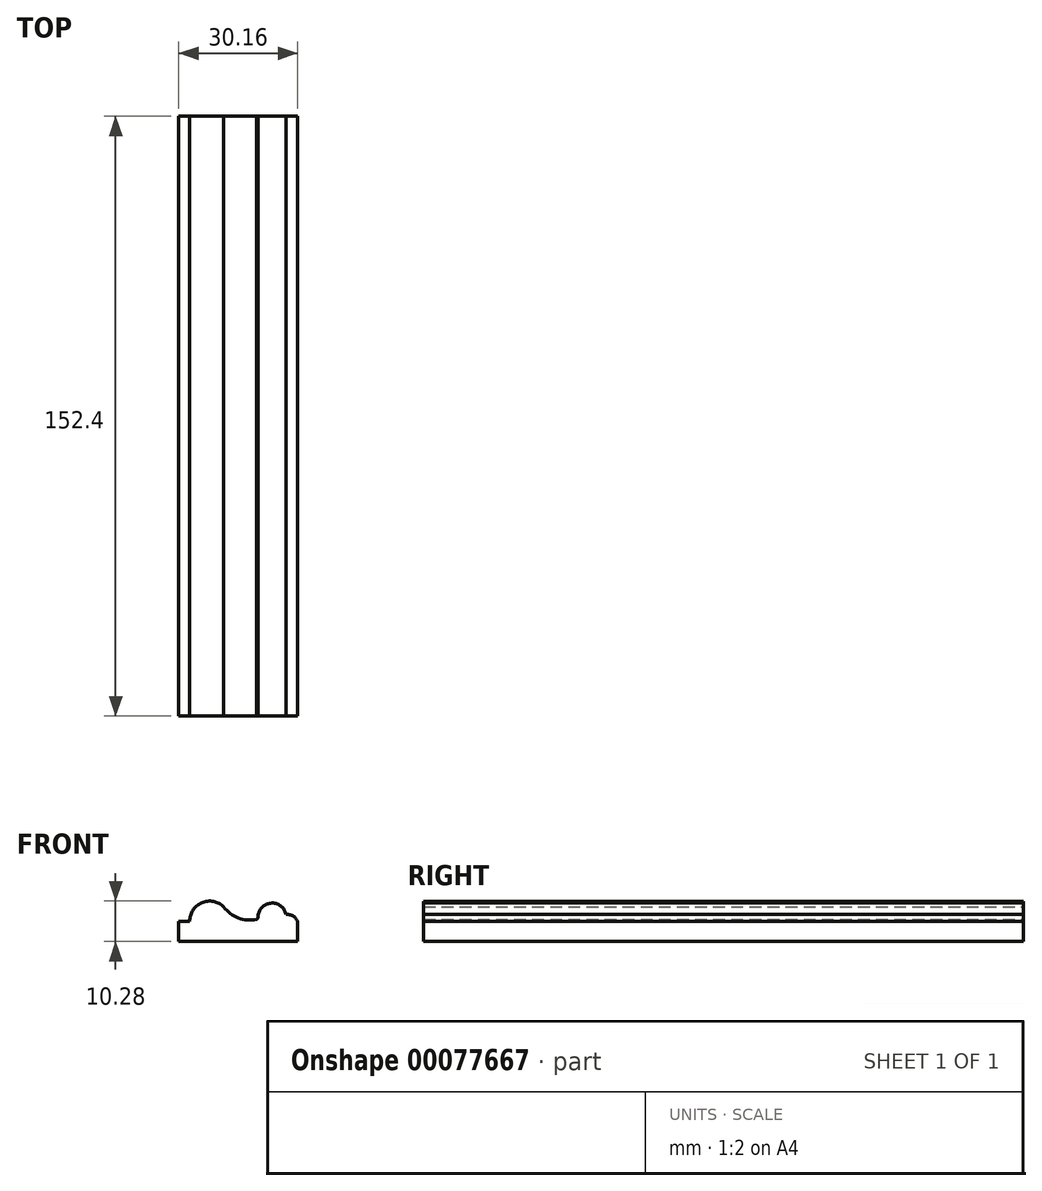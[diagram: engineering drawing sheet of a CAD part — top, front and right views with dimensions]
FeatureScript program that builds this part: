
annotation { "Feature Type Name" : "Feature", "Feature Type Description" : "" }
export const myFeature = defineFeature(function(context is Context, id is Id, definition is map)
    precondition{}
    {
        {
            var Q0;
            Q0=qCreatedBy(makeId("Front.planeOp"),FACE);
            var sketch = newSketch(context, id + "F0", { "sketchPlane" : qUnion([Q0])});
            skLineSegment(sketch, "E0", {"start": v(-15.08, -5.14) * mm, "end": v(-15.08, -0.06) * mm});
            skLineSegment(sketch, "E1", {"start": v(-15.08, -5.14) * mm, "end": v(15.08, -5.14) * mm});
            skLineSegment(sketch, "E2", {"start": v(15.08, -5.14) * mm, "end": v(15.08, 0) * mm});
            skLineSegment(sketch, "E3", {"start": v(-12.31, -0.06) * mm, "end": v(-15.08, -0.06) * mm});
            skArc(sketch, "E4", {"start": v(12.16, 1.72) * mm, "mid": v(8.26, 4.62) * mm, "end": v(5.02, 1) * mm});
            skArc(sketch, "E5", {"start": v(15.08, 0) * mm, "mid": v(13.91, 1.35) * mm, "end": v(12.16, 1.72) * mm});
            skArc(sketch, "E6", {"start": v(-3.66, 3.68) * mm, "mid": v(-9.24, 4.72) * mm, "end": v(-12.31, -0.06) * mm});
            skArc(sketch, "E7", {"start": v(-3.66, 3.68) * mm, "mid": v(0.02, 0.86) * mm, "end": v(4.65, 0.5) * mm});
            skArc(sketch, "E8", {"start": v(4.65, 0.5) * mm, "mid": v(4.92, 0.69) * mm, "end": v(5.02, 1) * mm});
            skSolve(sketch);
        }
        {
            var Q0;
            Q0=makeQuery(id+"F0.imprint","IMPRINT",FACE,{"disambiguationData":[TD([[makeQuery(id+"F0.imprint","IMPRINT",EDGE,{"derivedFrom":sQuery(id+"F0.wireOp",EDGE,"E1")}),1.0]])]});
            extrude(context, id + "F1", {"entities" : qUnion([Q0]), "depth" : 152.4 * mm});
        }
    });
